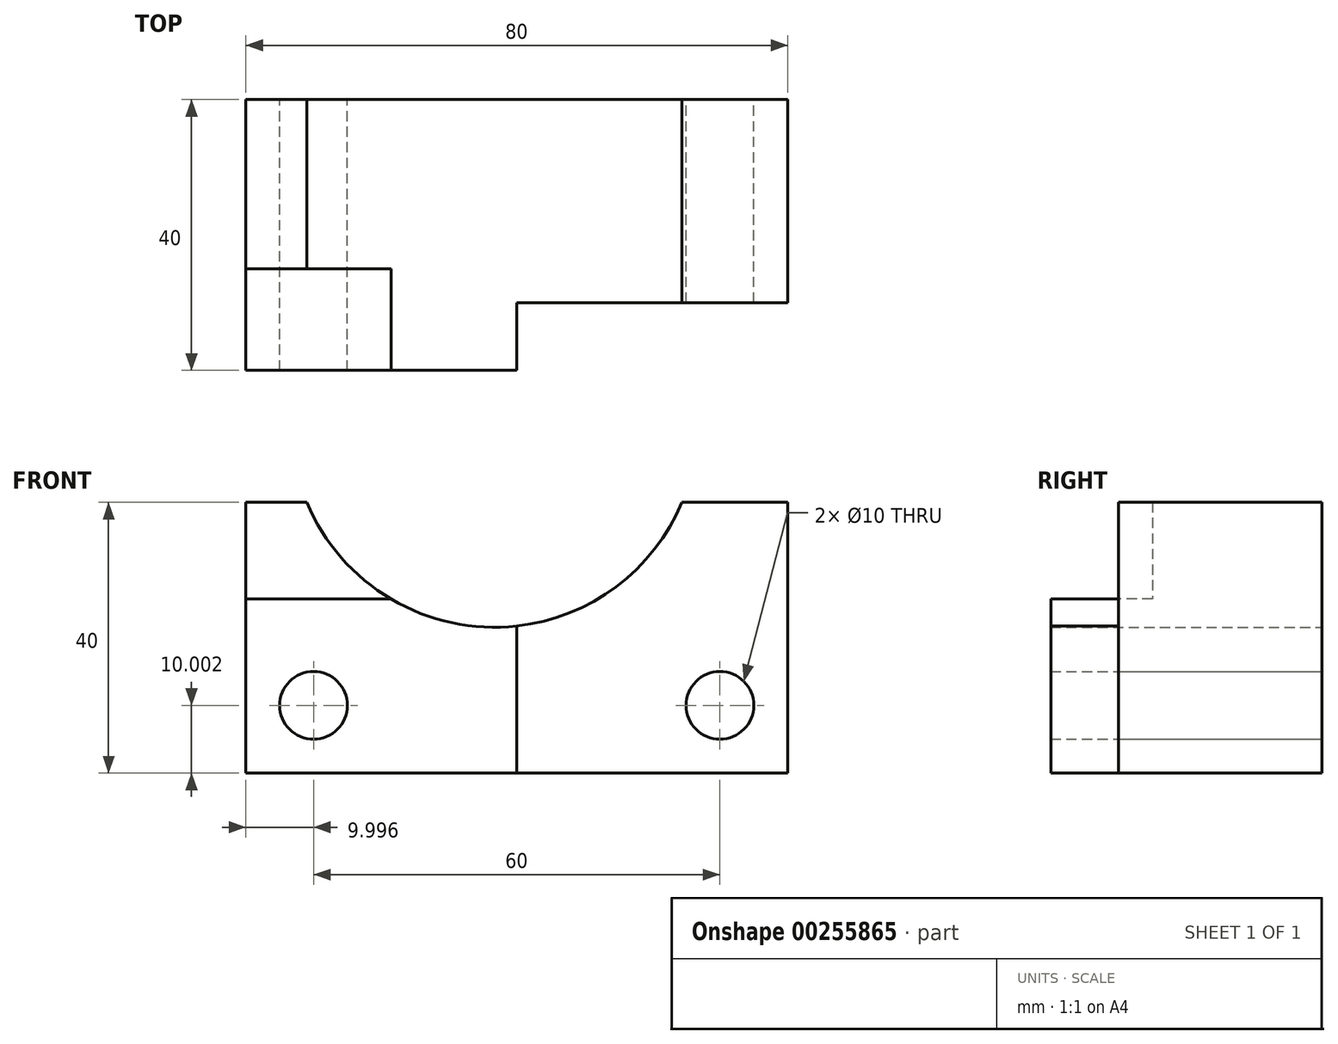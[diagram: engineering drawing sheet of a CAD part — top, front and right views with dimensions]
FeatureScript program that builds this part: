
annotation { "Feature Type Name" : "Feature", "Feature Type Description" : "" }
export const myFeature = defineFeature(function(context is Context, id is Id, definition is map)
    precondition{}
    {
        {
            var Q0;
            Q0=qCreatedBy(makeId("Front.planeOp"),FACE);
            var sketch = newSketch(context, id + "F0", { "sketchPlane" : qUnion([Q0])});
            skLineSegment(sketch, "E0.bottom", {"start": v(-32.45, 48.34) * mm, "end": v(-23.44, 48.34) * mm});
            skLineSegment(sketch, "E0.top", {"start": v(-32.45, 8.34) * mm, "end": v(47.55, 8.34) * mm});
            skLineSegment(sketch, "E0.left", {"start": v(-32.45, 48.34) * mm, "end": v(-32.45, 8.34) * mm});
            skLineSegment(sketch, "E0.right", {"start": v(47.55, 48.34) * mm, "end": v(47.55, 8.34) * mm});
            skArc(sketch, "E1", {"start": v(-23.44, 48.34) * mm, "mid": v(4.25, 29.88) * mm, "end": v(31.94, 48.34) * mm});
            skPoint(sketch, "E1.first.point", {"position": v(-23.44, 48.34) * mm});
            skPoint(sketch, "E1.second.point", {"position": v(31.94, 48.34) * mm});
            skPoint(sketch, "E1.third.point", {"position": v(4.12, 29.88) * mm});
            skLineSegment(sketch, "E2.trimOffspring", {"start": v(31.94, 48.34) * mm, "end": v(47.55, 48.34) * mm});
            skCircle(sketch, "E3", {"center": v(-22.45, 18.34) * mm, "radius": 5 * mm});
            skCircle(sketch, "E4", {"center": v(37.55, 18.34) * mm, "radius": 5 * mm});
            skSolve(sketch);
        }
        {
            var Q0;
            Q0=makeQuery(id+"F0.imprint","IMPRINT",FACE,{"disambiguationData":[TD([[makeQuery(id+"F0.imprint","IMPRINT",EDGE,{"derivedFrom":sQuery(id+"F0.wireOp",EDGE,"E0.bottom")}),-1.0]])]});
            extrude(context, id + "F1", {"entities" : qUnion([Q0]), "depth" : 40 * mm});
        }
        {
            var Q0;
            Q0=makeQuery(id+"F1.opExtrude","CAP_FACE",FACE,{"disambiguationData":[OSD([sQuery(id+"F0.wireOp",EDGE,"E0.bottom"),sQuery(id+"F0.wireOp",EDGE,"E0.top"),sQuery(id+"F0.wireOp",EDGE,"E0.left"),sQuery(id+"F0.wireOp",EDGE,"E0.right"),sQuery(id+"F0.wireOp",EDGE,"E1"),sQuery(id+"F0.wireOp",EDGE,"E2.trimOffspring"),sQuery(id+"F0.wireOp",EDGE,"E3"),sQuery(id+"F0.wireOp",EDGE,"E4")])],"isStart":false});
            var sketch = newSketch(context, id + "F2", { "sketchPlane" : qUnion([Q0])});
            skLineSegment(sketch, "E5", {"start": v(7.55, 30.06) * mm, "end": v(7.55, 8.34) * mm});
            skPoint(sketch, "E5.startSnap0", {"position": v(7.55, 8.34) * mm});
            skSolve(sketch);
        }
        {
            var Q0;
            {var subQ2=sQuery(id+"F2.wireOp",EDGE,"E5");Q0=makeQuery(id+"F2.imprint","IMPRINT",FACE,{"disambiguationData":[TD([[makeQuery(id+"F2.imprint","IMPRINT",EDGE,{"derivedFrom":subQ2}),1.0]])]});}
            extrude(context, id + "F3", {"entities" : qUnion([Q0]), "operationType" : NewBodyOperationType.REMOVE, "oppositeDirection" : true, "depth" : 10 * mm});
        }
        {
            var Q0;
            Q0=makeQuery(id+"F1.opExtrude","CAP_FACE",FACE,{"disambiguationData":[OSD([sQuery(id+"F0.wireOp",EDGE,"E0.bottom"),sQuery(id+"F0.wireOp",EDGE,"E0.top"),sQuery(id+"F0.wireOp",EDGE,"E0.left"),sQuery(id+"F0.wireOp",EDGE,"E0.right"),sQuery(id+"F0.wireOp",EDGE,"E1"),sQuery(id+"F0.wireOp",EDGE,"E2.trimOffspring"),sQuery(id+"F0.wireOp",EDGE,"E3"),sQuery(id+"F0.wireOp",EDGE,"E4")])],"isStart":false});
            var sketch = newSketch(context, id + "F4", { "sketchPlane" : qUnion([Q0])});
            skLineSegment(sketch, "E6", {"start": v(-11, 34.04) * mm, "end": v(-32.45, 34.04) * mm});
            skLineSegment(sketch, "E7", {"start": v(-32.45, 34.04) * mm, "end": v(-32.45, 48.34) * mm});
            skLineSegment(sketch, "E8", {"start": v(-32.45, 48.34) * mm, "end": v(-23.44, 48.34) * mm});
            skLineSegment(sketch, "E9", {"start": v(-23.44, 48.34) * mm, "end": v(-11, 34.04) * mm});
            skSolve(sketch);
        }
        {
            var Q0;
            {var subQ0=sQuery(id+"F4.wireOp",EDGE,"E9");Q0=makeQuery(id+"F4.imprint","IMPRINT",FACE,{"disambiguationData":[TD([[makeQuery(id+"F4.imprint","IMPRINT",EDGE,{"derivedFrom":subQ0}),-1.0]])]});}
            var Q1;
            {var subQ0=sQuery(id+"F4.wireOp",EDGE,"E6");Q1=makeQuery(id+"F4.imprint","IMPRINT",FACE,{"disambiguationData":[TD([[makeQuery(id+"F4.imprint","IMPRINT",EDGE,{"derivedFrom":subQ0}),-1.0]])]});}
            extrude(context, id + "F5", {"entities" : qUnion([Q0, Q1]), "operationType" : NewBodyOperationType.REMOVE, "oppositeDirection" : true, "depth" : 15 * mm});
        }
    });
